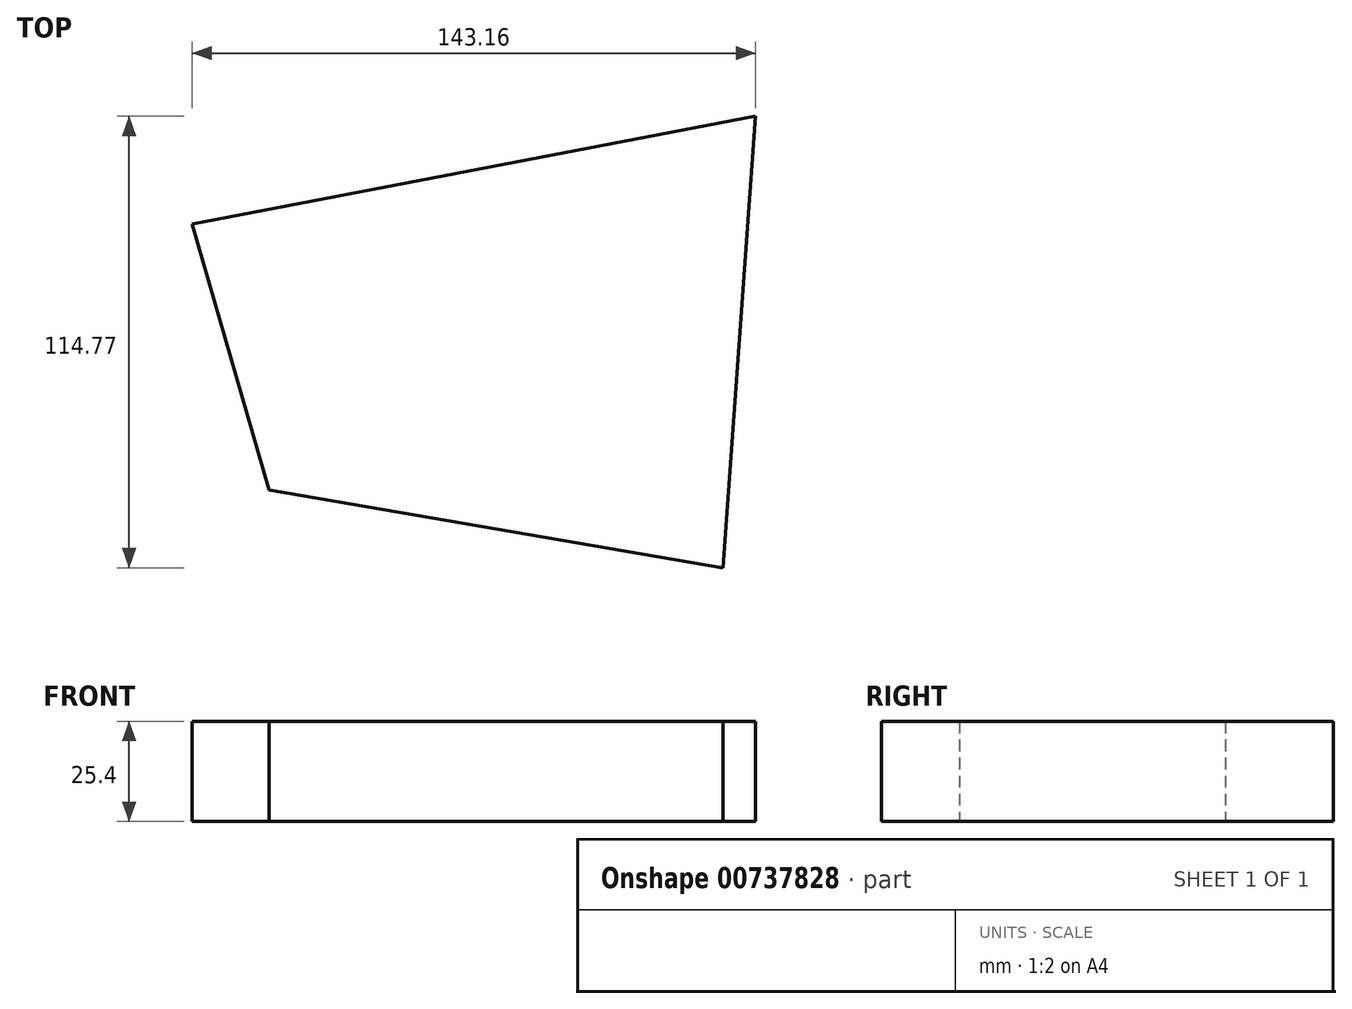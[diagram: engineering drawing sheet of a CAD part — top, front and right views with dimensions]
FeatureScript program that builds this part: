
annotation { "Feature Type Name" : "Feature", "Feature Type Description" : "" }
export const myFeature = defineFeature(function(context is Context, id is Id, definition is map)
    precondition{}
    {
        {
            var Q0;
            Q0=qCreatedBy(makeId("Top.planeOp"),FACE);
            var sketch = newSketch(context, id + "F0", { "sketchPlane" : qUnion([Q0])});
            skLineSegment(sketch, "E0", {"start": v(-67.79, 36.64) * mm, "end": v(75.84, 64.17) * mm});
            skLineSegment(sketch, "E1", {"start": v(75.84, 64.17) * mm, "end": v(67.5, -50.6) * mm});
            skLineSegment(sketch, "E2", {"start": v(67.5, -50.6) * mm, "end": v(-47.79, -30.83) * mm});
            skLineSegment(sketch, "E3", {"start": v(-47.79, -30.83) * mm, "end": v(-68.14, 39.56) * mm});
            skSolve(sketch);
        }
        {
            var Q0;
            Q0 = qSketchRegion(id + "F0", true);
            var sketch = newSketch(context, id + "F1", { "sketchPlane" : qUnion([Q0])});
            skSolve(sketch);
        }
        {
            var Q0;
            {var subQ0=sQuery(id+"F0.wireOp",EDGE,"E1");Q0=makeQuery(id+"F1.imprint","IMPRINT",FACE,{"disambiguationData":[TD([[makeQuery(id+"F1.imprint","IMPRINT",EDGE,{"derivedFrom":makeQuery(id+"F0.imprint","IMPRINT",EDGE,{"derivedFrom":subQ0})}),-1.0]])]});}
            extrude(context, id + "F2", {"entities" : qUnion([Q0]), "depth" : 25.4 * mm, "offsetDistance" : 25.4 * mm});
        }
    });
